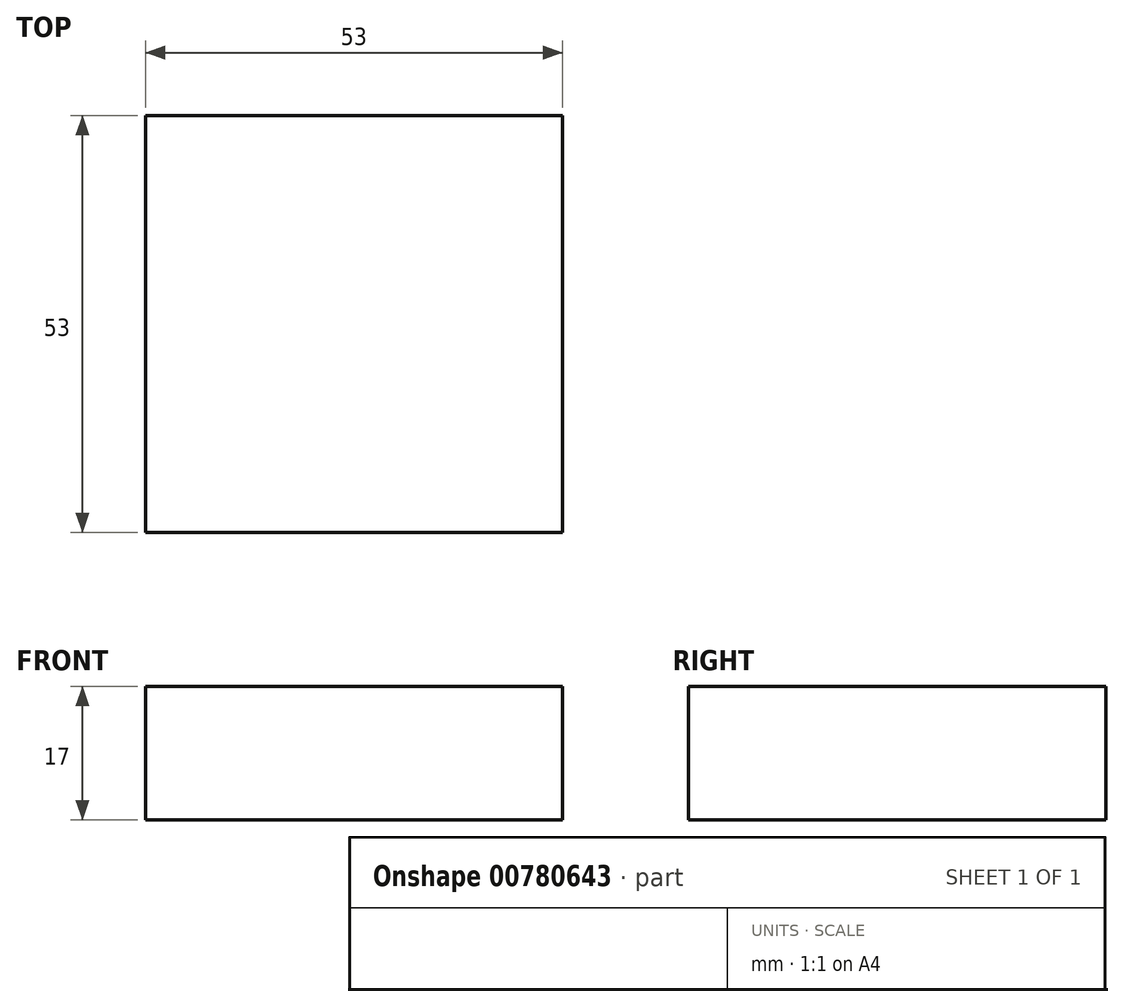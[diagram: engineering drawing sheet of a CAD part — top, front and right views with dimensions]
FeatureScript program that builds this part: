
annotation { "Feature Type Name" : "Feature", "Feature Type Description" : "" }
export const myFeature = defineFeature(function(context is Context, id is Id, definition is map)
    precondition{}
    {
        {
            var Q0;
            Q0=qCreatedBy(makeId("Top.planeOp"),FACE);
            var sketch = newSketch(context, id + "F0", { "sketchPlane" : qUnion([Q0])});
            skLineSegment(sketch, "E0.bottom", {"start": v(26.5, -26.5) * mm, "end": v(-26.5, -26.5) * mm});
            skLineSegment(sketch, "E0.top", {"start": v(26.5, 26.5) * mm, "end": v(-26.5, 26.5) * mm});
            skLineSegment(sketch, "E0.left", {"start": v(26.5, -26.5) * mm, "end": v(26.5, 26.5) * mm});
            skLineSegment(sketch, "E0.right", {"start": v(-26.5, -26.5) * mm, "end": v(-26.5, 26.5) * mm});
            skPoint(sketch, "E0.middle", {"position": v(0, 0) * mm});
            skSolve(sketch);
        }
        {
            var Q0;
            Q0=makeQuery(id+"F0.imprint","IMPRINT",FACE,{"disambiguationData":[TD([[makeQuery(id+"F0.imprint","IMPRINT",EDGE,{"derivedFrom":sQuery(id+"F0.wireOp",EDGE,"E0.bottom")}),-1.0]])]});
            extrude(context, id + "F1", {"entities" : qUnion([Q0]), "depth" : 17 * mm, "offsetDistance" : 25.4 * mm});
        }
    });
